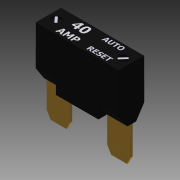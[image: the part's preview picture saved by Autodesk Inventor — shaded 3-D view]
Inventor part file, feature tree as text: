
AUTODESK INVENTOR PART (.ipt)
format: ipt  version: 2016 SP1 (Build 200210100, 210)  size: 482,816 bytes
history: native  units: in
note: dims shown in document units (in); Inventor stores cm internally (conversion verified against a paired STEP export)
features: sketch x7, chamfer x6, extrude x5, plane x5, mirror x4, emboss x2, split x1, fillet x1
ambient origin geometry x8: Origin, YZ Plane, XZ Plane, XY Plane, X Axis, Y Axis, Z Axis, Center Point
bodies: Solid1 (feature_tree)
feature tree (31):
  extrude  "Extrusion1"  Depth=0.72in
  extrude  "Extrusion2"  Depth=0.18in
  plane  "Work Plane1"
  mirror  "Mirror1"
  plane  "Work Plane2"
  mirror  "Mirror2"
  extrude  "Extrusion4"  Depth=0.28in TaperAngle=0.0deg
  chamfer  "Chamfer1"  Distance=0.49in
  chamfer  "Chamfer2"  Distance=0.1in Angle=45.0deg
  chamfer  "Chamfer3"  Distance=0.1in Angle=45.0deg
  chamfer  "Chamfer4"  Distance=0.1in Angle=45.0deg
  plane  "Work Plane3"
  mirror  "Mirror3"
  chamfer  "Chamfer5"  Distance=0.1in Angle=45.0deg
  chamfer  "Chamfer6"  Distance=0.05in Angle=45.0deg
  split  "Split1"
  extrude  "Extrusion5"  Depth=0.03in
  plane  "Work Plane4"
  emboss  "Emboss1"
  fillet  "Fillet1"  Radius=0.025in
  plane  "Work Plane5"
  emboss  "Emboss4"
  extrude  "Extrusion7"  Depth=0.03in
  mirror  "Mirror4"
  sketch  "Sketch1"  dims[d0=1.14in d1=0.72in]
  sketch  "Sketch2"  dims[d2=0.35in d3=0.0in d4=0.18in]
  sketch  "Sketch4"  dims[d5=0.1167in d6=0.28in d7=0.0in]
  sketch  "Sketch5"  dims[d13=0.315in]
  sketch  "Sketch6"  dims[d14=0.032in d15=0.49in d16=0.0in d17=0.1in d18=0.05in d19=45.0deg d20=0.1in d21=0.05in d22=45.0deg d23=0.1in d24=0.005in d25=45.0deg d26=0.1in d27=0.005in d28=45.0deg]
  sketch  "Sketch9"  dims[d29=0.0in d30=0.05in d31=0.1in d32=45.0deg]
  sketch  "Sketch10"  dims[d33=0.05in d34=0.1in d35=45.0deg d36=0.125in d37=0.025in d38=0.0in d39=0.1875in d41=0.001in d42=0.0in d43=0.01in d50=0.125in d51=0.0001in d52=0.0in d53=0.03in d56=1.0in d57=0.0in d58=0.456in d59=0.456in]
